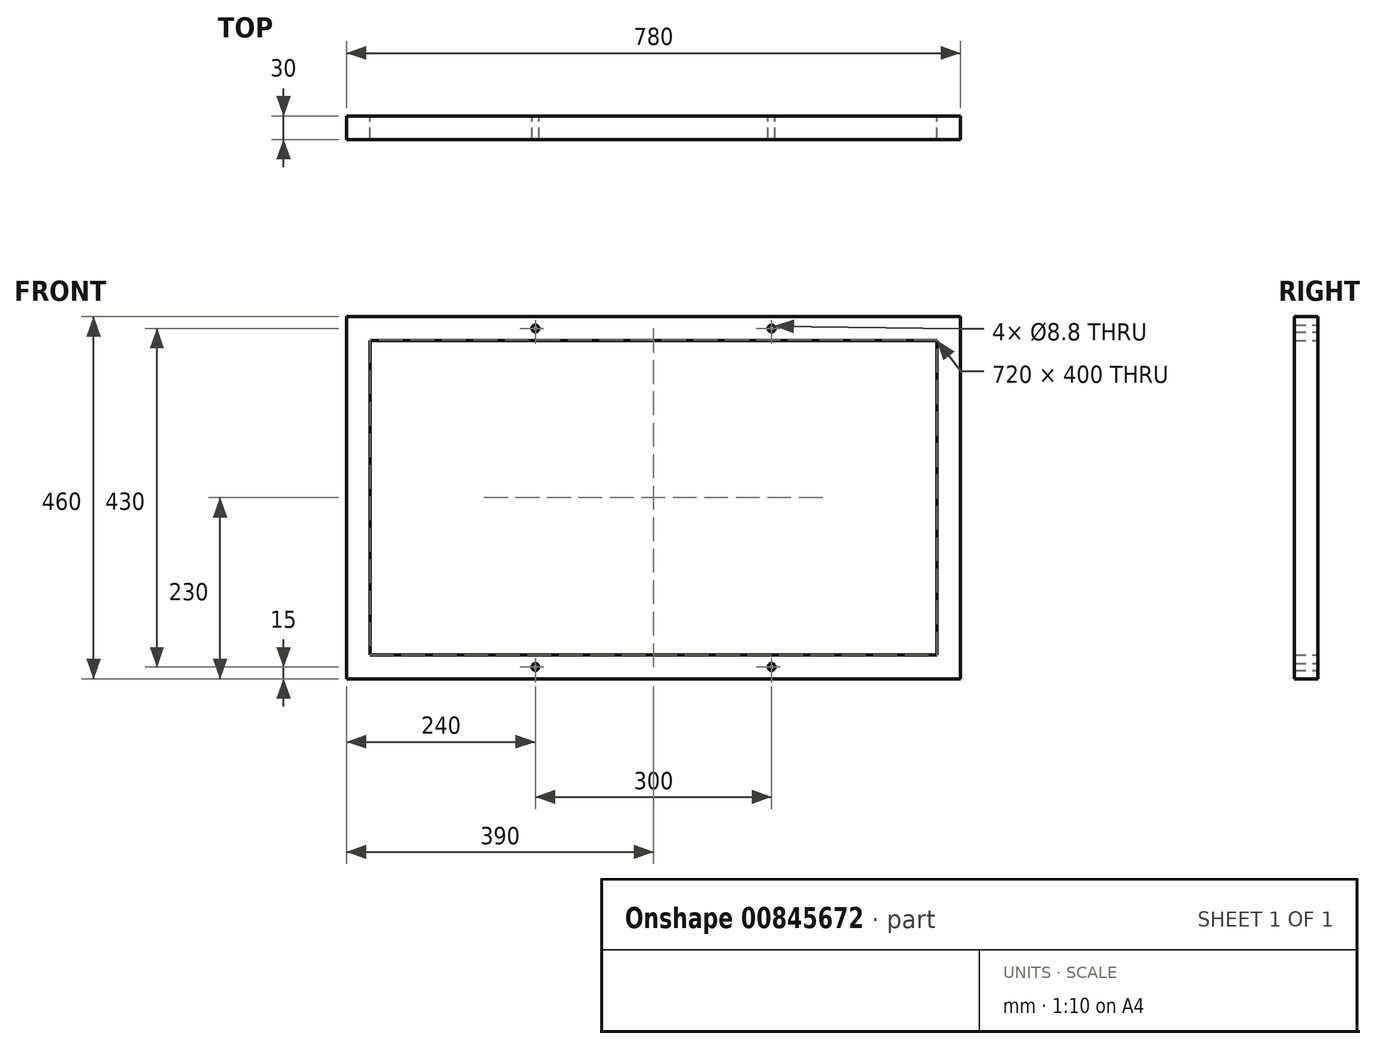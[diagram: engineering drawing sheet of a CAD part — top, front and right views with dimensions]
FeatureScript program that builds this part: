
annotation { "Feature Type Name" : "Feature", "Feature Type Description" : "" }
export const myFeature = defineFeature(function(context is Context, id is Id, definition is map)
    precondition{}
    {
        {
            var Q0;
            Q0=qCreatedBy(makeId("Front.planeOp"),FACE);
            var sketch = newSketch(context, id + "F0", { "sketchPlane" : qUnion([Q0])});
            skLineSegment(sketch, "E0.bottom", {"start": v(0, 0) * mm, "end": v(780, 0) * mm});
            skLineSegment(sketch, "E0.top", {"start": v(0, 460) * mm, "end": v(780, 460) * mm});
            skLineSegment(sketch, "E0.left", {"start": v(0, 0) * mm, "end": v(0, 460) * mm});
            skLineSegment(sketch, "E0.right", {"start": v(780, 0) * mm, "end": v(780, 460) * mm});
            skLineSegment(sketch, "E1.0", {"start": v(30, 430) * mm, "end": v(750, 430) * mm});
            skLineSegment(sketch, "E1.1", {"start": v(30, 30) * mm, "end": v(30, 430) * mm});
            skLineSegment(sketch, "E1.2", {"start": v(30, 30) * mm, "end": v(750, 30) * mm});
            skLineSegment(sketch, "E1.3", {"start": v(750, 30) * mm, "end": v(750, 430) * mm});
            skPoint(sketch, "E2", {"position": v(240, 445) * mm});
            skPoint(sketch, "E3", {"position": v(540, 445) * mm});
            skPoint(sketch, "E4", {"position": v(240, 15) * mm});
            skPoint(sketch, "E5", {"position": v(540, 15) * mm});
            skSolve(sketch);
        }
        {
            var Q0;
            Q0=makeQuery(id+"F0.imprint","IMPRINT",FACE,{"disambiguationData":[TD([[makeQuery(id+"F0.imprint","IMPRINT",EDGE,{"derivedFrom":sQuery(id+"F0.wireOp",EDGE,"E0.bottom")}),1.0]])]});
            extrude(context, id + "F1", {"entities" : qUnion([Q0]), "depth" : 30 * mm, "offsetDistance" : 25 * mm});
        }
        {
            var Q0;
            Q0=sQuery(id+"F0.wireOp",VERTEX,"E2");
            var Q1;
            Q1=sQuery(id+"F0.wireOp",VERTEX,"E3");
            var Q2;
            Q2=sQuery(id+"F0.wireOp",VERTEX,"E5");
            var Q3;
            Q3=sQuery(id+"F0.wireOp",VERTEX,"E4");
            var Q4;
            Q4=makeQuery(id+"F1.opExtrude","SWEPT_BODY",BODY,{"disambiguationData":[OSD([sQuery(id+"F0.wireOp",EDGE,"E0.bottom"),sQuery(id+"F0.wireOp",EDGE,"E0.top"),sQuery(id+"F0.wireOp",EDGE,"E0.left"),sQuery(id+"F0.wireOp",EDGE,"E0.right"),sQuery(id+"F0.wireOp",EDGE,"E1.0"),sQuery(id+"F0.wireOp",EDGE,"E1.1"),sQuery(id+"F0.wireOp",EDGE,"E1.2"),sQuery(id+"F0.wireOp",EDGE,"E1.3")])]});
            hole(context, id + "F2", {"style" : HoleStyle.SIMPLE, "endStyle" : HoleEndStyle.THROUGH, "oppositeDirection" : true, "standardTappedOrClearance" : lookupTablePath({ "fit" : "Normal", "standard" : "ISO", "size" : "M8", "type" : "Clearance" }), "standardBlindInLast" : lookupTablePath({ "fit" : "Standard", "standard" : "ISO", "size" : "M8", "type" : "Clearance" }), "holeDiameter" : 8.8 * mm, "majorDiameter" : 5 * mm, "isTappedThrough" : true, "tappedDepth" : 12 * mm, "tapClearance" : 3, "locations" : qUnion([Q0, Q1, Q2, Q3]), "scope" : qUnion([Q4])});
        }
    });
